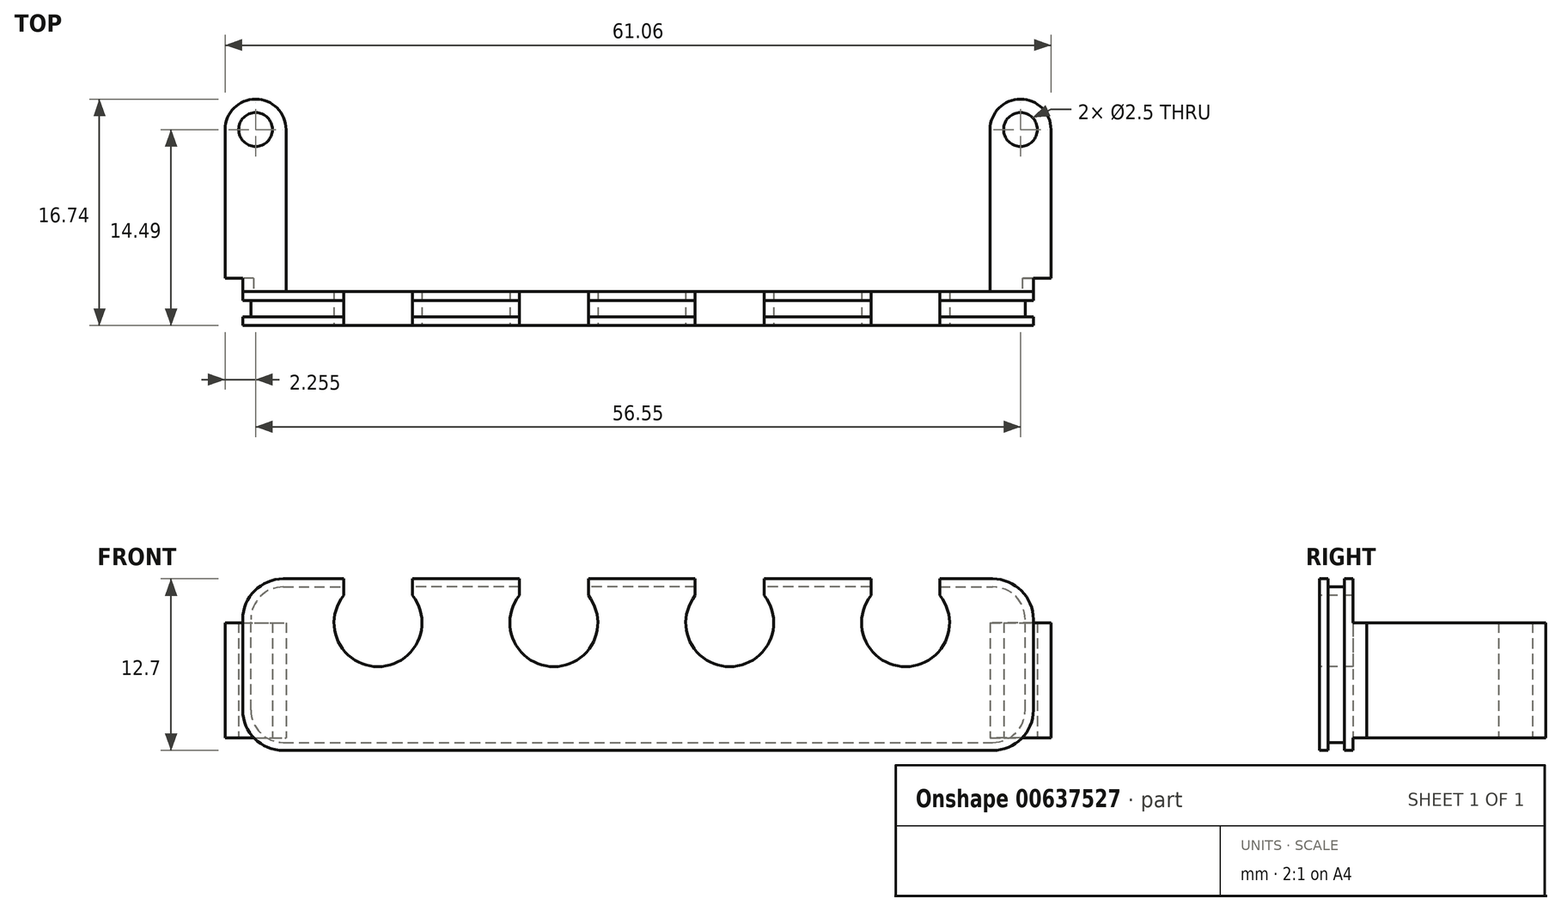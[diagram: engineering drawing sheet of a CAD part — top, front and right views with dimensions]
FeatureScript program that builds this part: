
annotation { "Feature Type Name" : "Feature", "Feature Type Description" : "" }
export const myFeature = defineFeature(function(context is Context, id is Id, definition is map)
    precondition{}
    {
        {
            var Q0;
            Q0=qCreatedBy(makeId("Front.planeOp"),FACE);
            var sketch = newSketch(context, id + "F0", { "sketchPlane" : qUnion([Q0])});
            skLineSegment(sketch, "E0.bottom", {"start": v(-26.22, -6.35) * mm, "end": v(26.23, -6.35) * mm});
            skLineSegment(sketch, "E0.top", {"start": v(-26.23, 6.35) * mm, "end": v(-21.77, 6.35) * mm});
            skLineSegment(sketch, "E0.left", {"start": v(-29.23, -3.35) * mm, "end": v(-29.23, 3.35) * mm});
            skLineSegment(sketch, "E0.right", {"start": v(29.23, -3.35) * mm, "end": v(29.23, 3.35) * mm});
            skPoint(sketch, "E0.middle", {"position": v(0, 0) * mm});
            skPoint(sketch, "E1.visualSharp", {"position": v(-29.23, 6.35) * mm});
            skArc(sketch, "E1.filletArc", {"start": v(-26.23, 6.35) * mm, "mid": v(-28.35, 5.47) * mm, "end": v(-29.23, 3.35) * mm});
            skPoint(sketch, "E2.visualSharp", {"position": v(-29.23, -6.35) * mm});
            skArc(sketch, "E2.filletArc", {"start": v(-29.23, -3.35) * mm, "mid": v(-28.35, -5.47) * mm, "end": v(-26.22, -6.35) * mm});
            skPoint(sketch, "E3.visualSharp", {"position": v(29.23, -6.35) * mm});
            skArc(sketch, "E3.filletArc", {"start": v(26.23, -6.35) * mm, "mid": v(28.35, -5.47) * mm, "end": v(29.23, -3.35) * mm});
            skPoint(sketch, "E4.visualSharp", {"position": v(29.23, 6.35) * mm});
            skArc(sketch, "E4.filletArc", {"start": v(29.23, 3.35) * mm, "mid": v(28.35, 5.47) * mm, "end": v(26.23, 6.35) * mm});
            skArc(sketch, "E5", {"start": v(-21.78, 5.11) * mm, "mid": v(-19.22, -0.15) * mm, "end": v(-16.67, 5.11) * mm});
            skArc(sketch, "E6", {"start": v(-8.78, 5.11) * mm, "mid": v(-6.22, -0.15) * mm, "end": v(-3.67, 5.11) * mm});
            skArc(sketch, "E7", {"start": v(4.22, 5.11) * mm, "mid": v(6.78, -0.15) * mm, "end": v(9.33, 5.11) * mm});
            skArc(sketch, "E8", {"start": v(17.22, 5.11) * mm, "mid": v(19.78, -0.15) * mm, "end": v(22.33, 5.11) * mm});
            skLineSegment(sketch, "E9.left", {"start": v(-21.77, 5.11) * mm, "end": v(-21.77, 6.35) * mm});
            skLineSegment(sketch, "E9.right", {"start": v(-16.67, 5.11) * mm, "end": v(-16.67, 6.35) * mm});
            skLineSegment(sketch, "E10.1.0.1", {"start": v(-8.77, 5.11) * mm, "end": v(-8.77, 6.35) * mm});
            skLineSegment(sketch, "E10.1.0.2", {"start": v(-3.67, 5.11) * mm, "end": v(-3.67, 6.35) * mm});
            skLineSegment(sketch, "E10.2.0.1", {"start": v(4.23, 5.11) * mm, "end": v(4.23, 6.35) * mm});
            skLineSegment(sketch, "E10.2.0.2", {"start": v(9.33, 5.11) * mm, "end": v(9.33, 6.35) * mm});
            skLineSegment(sketch, "E10.3.0.1", {"start": v(17.23, 5.11) * mm, "end": v(17.23, 6.35) * mm});
            skLineSegment(sketch, "E10.3.0.2", {"start": v(22.33, 5.11) * mm, "end": v(22.33, 6.35) * mm});
            skLineSegment(sketch, "E11.trimOffspring", {"start": v(-16.67, 6.35) * mm, "end": v(-8.77, 6.35) * mm});
            skLineSegment(sketch, "E12.trimOffspring", {"start": v(-3.67, 6.35) * mm, "end": v(4.23, 6.35) * mm});
            skLineSegment(sketch, "E13.trimOffspring", {"start": v(9.33, 6.35) * mm, "end": v(17.23, 6.35) * mm});
            skLineSegment(sketch, "E14.trimOffspring", {"start": v(22.33, 6.35) * mm, "end": v(26.23, 6.35) * mm});
            skSolve(sketch);
        }
        {
            var Q0;
            Q0=makeQuery(id+"F0.imprint","IMPRINT",FACE,{"disambiguationData":[TD([[makeQuery(id+"F0.imprint","IMPRINT",EDGE,{"derivedFrom":sQuery(id+"F0.wireOp",EDGE,"E0.bottom")}),1.0]])]});
            extrude(context, id + "F1", {"entities" : qUnion([Q0]), "oppositeDirection" : true, "depth" : 0.64 * mm, "offsetDistance" : 25 * mm});
        }
        {
            var Q0;
            Q0=makeQuery(id+"F1.opExtrude","CAP_FACE",FACE,{"disambiguationData":[OSD([sQuery(id+"F0.wireOp",EDGE,"E0.bottom"),sQuery(id+"F0.wireOp",EDGE,"E0.top"),sQuery(id+"F0.wireOp",EDGE,"E0.left"),sQuery(id+"F0.wireOp",EDGE,"E0.right"),sQuery(id+"F0.wireOp",EDGE,"E1.filletArc"),sQuery(id+"F0.wireOp",EDGE,"E2.filletArc"),sQuery(id+"F0.wireOp",EDGE,"E3.filletArc"),sQuery(id+"F0.wireOp",EDGE,"E4.filletArc"),sQuery(id+"F0.wireOp",EDGE,"E5"),sQuery(id+"F0.wireOp",EDGE,"E6"),sQuery(id+"F0.wireOp",EDGE,"E7"),sQuery(id+"F0.wireOp",EDGE,"E8"),sQuery(id+"F0.wireOp",EDGE,"E9.left"),sQuery(id+"F0.wireOp",EDGE,"E9.right"),sQuery(id+"F0.wireOp",EDGE,"E10.1.0.1"),sQuery(id+"F0.wireOp",EDGE,"E10.1.0.2"),sQuery(id+"F0.wireOp",EDGE,"E10.2.0.1"),sQuery(id+"F0.wireOp",EDGE,"E10.2.0.2"),sQuery(id+"F0.wireOp",EDGE,"E10.3.0.1"),sQuery(id+"F0.wireOp",EDGE,"E10.3.0.2"),sQuery(id+"F0.wireOp",EDGE,"E11.trimOffspring"),sQuery(id+"F0.wireOp",EDGE,"E12.trimOffspring"),sQuery(id+"F0.wireOp",EDGE,"E13.trimOffspring"),sQuery(id+"F0.wireOp",EDGE,"E14.trimOffspring")])],"isStart":false});
            var sketch = newSketch(context, id + "F2", { "sketchPlane" : qUnion([Q0])});
            skLineSegment(sketch, "E15.0", {"start": v(-22.33, 5.75) * mm, "end": v(-26.23, 5.75) * mm});
            skArc(sketch, "E15.1", {"start": v(-28.62, 3.35) * mm, "mid": v(-27.92, 5.05) * mm, "end": v(-26.23, 5.75) * mm});
            skLineSegment(sketch, "E15.2", {"start": v(-28.62, -3.35) * mm, "end": v(-28.62, 3.35) * mm});
            skArc(sketch, "E15.3", {"start": v(-26.23, -5.75) * mm, "mid": v(-27.92, -5.05) * mm, "end": v(-28.62, -3.35) * mm});
            skLineSegment(sketch, "E15.4", {"start": v(26.23, -5.75) * mm, "end": v(-26.23, -5.75) * mm});
            skLineSegment(sketch, "E15.5", {"start": v(26.23, 5.75) * mm, "end": v(21.77, 5.75) * mm});
            skArc(sketch, "E15.6", {"start": v(26.23, 5.75) * mm, "mid": v(27.92, 5.05) * mm, "end": v(28.62, 3.35) * mm});
            skLineSegment(sketch, "E15.7", {"start": v(28.62, -3.35) * mm, "end": v(28.62, 3.35) * mm});
            skArc(sketch, "E15.8", {"start": v(28.62, -3.35) * mm, "mid": v(27.92, -5.05) * mm, "end": v(26.23, -5.75) * mm});
            skArc(sketch, "E16", {"start": v(-22.33, 5.11) * mm, "mid": v(-19.78, -0.15) * mm, "end": v(-17.23, 5.11) * mm});
            skArc(sketch, "E17", {"start": v(-9.33, 5.11) * mm, "mid": v(-6.77, -0.15) * mm, "end": v(-4.23, 5.11) * mm});
            skArc(sketch, "E18", {"start": v(3.67, 5.11) * mm, "mid": v(6.23, -0.15) * mm, "end": v(8.77, 5.11) * mm});
            skArc(sketch, "E19", {"start": v(16.67, 5.11) * mm, "mid": v(19.23, -0.15) * mm, "end": v(21.77, 5.11) * mm});
            skLineSegment(sketch, "E20.left", {"start": v(-17.23, 5.75) * mm, "end": v(-17.23, 5.11) * mm});
            skLineSegment(sketch, "E20.right", {"start": v(-22.33, 5.75) * mm, "end": v(-22.33, 5.11) * mm});
            skLineSegment(sketch, "E21.left", {"start": v(-4.23, 5.75) * mm, "end": v(-4.23, 5.11) * mm});
            skLineSegment(sketch, "E21.right", {"start": v(-9.33, 5.75) * mm, "end": v(-9.33, 5.11) * mm});
            skLineSegment(sketch, "E22.left", {"start": v(8.77, 5.75) * mm, "end": v(8.77, 5.11) * mm});
            skLineSegment(sketch, "E22.right", {"start": v(3.67, 5.75) * mm, "end": v(3.67, 5.11) * mm});
            skLineSegment(sketch, "E23.left", {"start": v(21.77, 5.75) * mm, "end": v(21.78, 5.11) * mm});
            skLineSegment(sketch, "E23.right", {"start": v(16.67, 5.75) * mm, "end": v(16.67, 5.11) * mm});
            skLineSegment(sketch, "E24.trimOffspring", {"start": v(-17.23, 5.75) * mm, "end": v(-9.33, 5.75) * mm});
            skLineSegment(sketch, "E25.trimOffspring", {"start": v(-4.23, 5.75) * mm, "end": v(3.67, 5.75) * mm});
            skLineSegment(sketch, "E26.trimOffspring", {"start": v(8.77, 5.75) * mm, "end": v(16.67, 5.75) * mm});
            skSolve(sketch);
        }
        {
            var Q0;
            Q0=qSketchRegion(id+"F2",true);
            extrude(context, id + "F3", {"entities" : qUnion([Q0]), "operationType" : NewBodyOperationType.ADD, "depth" : 1.21 * mm, "offsetDistance" : 25 * mm});
        }
        {
            var Q0;
            Q0=makeQuery(id+"F3.opExtrude","CAP_FACE",FACE,{"disambiguationData":[OSD([sQuery(id+"F2.wireOp",EDGE,"E15.0"),sQuery(id+"F2.wireOp",EDGE,"E15.1"),sQuery(id+"F2.wireOp",EDGE,"E15.2"),sQuery(id+"F2.wireOp",EDGE,"E15.3"),sQuery(id+"F2.wireOp",EDGE,"E15.4"),sQuery(id+"F2.wireOp",EDGE,"E15.5"),sQuery(id+"F2.wireOp",EDGE,"E15.6"),sQuery(id+"F2.wireOp",EDGE,"E15.7"),sQuery(id+"F2.wireOp",EDGE,"E15.8"),sQuery(id+"F2.wireOp",EDGE,"E16"),sQuery(id+"F2.wireOp",EDGE,"E17"),sQuery(id+"F2.wireOp",EDGE,"E18"),sQuery(id+"F2.wireOp",EDGE,"E19"),sQuery(id+"F2.wireOp",EDGE,"E20.left"),sQuery(id+"F2.wireOp",EDGE,"E20.right"),sQuery(id+"F2.wireOp",EDGE,"E21.left"),sQuery(id+"F2.wireOp",EDGE,"E21.right"),sQuery(id+"F2.wireOp",EDGE,"E22.left"),sQuery(id+"F2.wireOp",EDGE,"E22.right"),sQuery(id+"F2.wireOp",EDGE,"E23.left"),sQuery(id+"F2.wireOp",EDGE,"E23.right"),sQuery(id+"F2.wireOp",EDGE,"E24.trimOffspring"),sQuery(id+"F2.wireOp",EDGE,"E25.trimOffspring"),sQuery(id+"F2.wireOp",EDGE,"E26.trimOffspring")])],"isStart":false});
            var sketch = newSketch(context, id + "F4", { "sketchPlane" : qUnion([Q0])});
            skLineSegment(sketch, "E27.bottom", {"start": v(-26.22, -6.35) * mm, "end": v(26.23, -6.35) * mm});
            skLineSegment(sketch, "E27.top", {"start": v(-26.23, 6.35) * mm, "end": v(-22.33, 6.35) * mm});
            skLineSegment(sketch, "E27.left", {"start": v(-29.23, -3.35) * mm, "end": v(-29.23, 3.35) * mm});
            skLineSegment(sketch, "E27.right", {"start": v(29.23, -3.35) * mm, "end": v(29.23, 3.35) * mm});
            skPoint(sketch, "E27.middle", {"position": v(0, 0) * mm});
            skPoint(sketch, "E28.visualSharp", {"position": v(-29.23, 6.35) * mm});
            skArc(sketch, "E28.filletArc", {"start": v(-26.23, 6.35) * mm, "mid": v(-28.35, 5.47) * mm, "end": v(-29.23, 3.35) * mm});
            skPoint(sketch, "E29.visualSharp", {"position": v(-29.23, -6.35) * mm});
            skArc(sketch, "E29.filletArc", {"start": v(-29.22, -3.35) * mm, "mid": v(-28.35, -5.47) * mm, "end": v(-26.22, -6.35) * mm});
            skPoint(sketch, "E30.visualSharp", {"position": v(29.23, -6.35) * mm});
            skArc(sketch, "E30.filletArc", {"start": v(26.23, -6.35) * mm, "mid": v(28.35, -5.47) * mm, "end": v(29.23, -3.35) * mm});
            skPoint(sketch, "E31.visualSharp", {"position": v(29.23, 6.35) * mm});
            skArc(sketch, "E31.filletArc", {"start": v(29.23, 3.35) * mm, "mid": v(28.35, 5.47) * mm, "end": v(26.23, 6.35) * mm});
            skArc(sketch, "E32", {"start": v(-22.33, 5.11) * mm, "mid": v(-19.77, -0.15) * mm, "end": v(-17.23, 5.11) * mm});
            skArc(sketch, "E33", {"start": v(-9.33, 5.11) * mm, "mid": v(-6.77, -0.15) * mm, "end": v(-4.22, 5.11) * mm});
            skArc(sketch, "E34", {"start": v(3.67, 5.11) * mm, "mid": v(6.23, -0.15) * mm, "end": v(8.78, 5.11) * mm});
            skArc(sketch, "E35", {"start": v(16.67, 5.11) * mm, "mid": v(19.23, -0.15) * mm, "end": v(21.78, 5.11) * mm});
            skLineSegment(sketch, "E36.left", {"start": v(-22.33, 5.11) * mm, "end": v(-22.33, 6.35) * mm});
            skLineSegment(sketch, "E36.right", {"start": v(-17.23, 5.11) * mm, "end": v(-17.23, 6.35) * mm});
            skLineSegment(sketch, "E37.1.0.1", {"start": v(-9.33, 5.11) * mm, "end": v(-9.33, 6.35) * mm});
            skLineSegment(sketch, "E37.1.0.2", {"start": v(-4.22, 5.11) * mm, "end": v(-4.22, 6.35) * mm});
            skLineSegment(sketch, "E37.2.0.1", {"start": v(3.67, 5.11) * mm, "end": v(3.67, 6.35) * mm});
            skLineSegment(sketch, "E37.2.0.2", {"start": v(8.78, 5.11) * mm, "end": v(8.78, 6.35) * mm});
            skLineSegment(sketch, "E37.3.0.1", {"start": v(16.67, 5.11) * mm, "end": v(16.67, 6.35) * mm});
            skLineSegment(sketch, "E37.3.0.2", {"start": v(21.78, 5.11) * mm, "end": v(21.78, 6.35) * mm});
            skLineSegment(sketch, "E38.trimOffspring", {"start": v(-17.23, 6.35) * mm, "end": v(-9.33, 6.35) * mm});
            skLineSegment(sketch, "E39.trimOffspring", {"start": v(-4.22, 6.35) * mm, "end": v(3.67, 6.35) * mm});
            skLineSegment(sketch, "E40.trimOffspring", {"start": v(8.78, 6.35) * mm, "end": v(16.67, 6.35) * mm});
            skLineSegment(sketch, "E41.trimOffspring", {"start": v(21.78, 6.35) * mm, "end": v(26.23, 6.35) * mm});
            skSolve(sketch);
        }
        {
            var Q0;
            Q0=qSketchRegion(id+"F4",true);
            extrude(context, id + "F5", {"entities" : qUnion([Q0]), "operationType" : NewBodyOperationType.ADD, "depth" : 0.64 * mm, "offsetDistance" : 25 * mm});
        }
        {
            var Q0;
            Q0=makeQuery(id+"F5.opExtrude","SWEPT_FACE",FACE,{"disambiguationData":[OSD([sQuery(id+"F4.wireOp",EDGE,"E27.bottom")])]});
            cPlane(context, id + "F6", {"entities" : qUnion([Q0]), "cplaneType" : CPlaneType.OFFSET, "offset" : 0.95 * mm, "oppositeDirection" : true, "width" : 150 * mm, "height" : 150 * mm});
        }
        {
            var Q0;
            Q0=qCreatedBy(id+"F6.planeOp",FACE);
            var sketch = newSketch(context, id + "F7", { "sketchPlane" : qUnion([Q0])});
            skLineSegment(sketch, "E42.bottom", {"start": v(29.23, -2.5) * mm, "end": v(26.02, -2.5) * mm});
            skLineSegment(sketch, "E42.left", {"start": v(29.23, -2.5) * mm, "end": v(29.23, -3.49) * mm});
            skLineSegment(sketch, "E42.right", {"start": v(26.02, -2.5) * mm, "end": v(26.02, -3.49) * mm});
            skLineSegment(sketch, "E43.bottom", {"start": v(29.23, -3.49) * mm, "end": v(30.52, -3.49) * mm});
            skLineSegment(sketch, "E43.left", {"start": v(26.02, -3.49) * mm, "end": v(26.02, -14.5) * mm});
            skLineSegment(sketch, "E43.right", {"start": v(30.52, -3.49) * mm, "end": v(30.52, -14.5) * mm});
            skArc(sketch, "E44", {"start": v(26.02, -14.5) * mm, "mid": v(28.28, -16.74) * mm, "end": v(30.53, -14.5) * mm});
            skCircle(sketch, "E45", {"center": v(28.28, -14.5) * mm, "radius": 1.25 * mm});
            skLineSegment(sketch, "E46.MirrorCS", {"start": v(-26.02, -3.49) * mm, "end": v(-26.02, -14.5) * mm});
            skLineSegment(sketch, "E47.MirrorCS", {"start": v(-30.52, -3.49) * mm, "end": v(-30.52, -14.5) * mm});
            skCircle(sketch, "E48.MirrorC", {"center": v(-28.28, -14.5) * mm, "radius": 1.25 * mm});
            skArc(sketch, "E49.MirrorCS", {"start": v(-26.02, -14.5) * mm, "mid": v(-28.28, -16.74) * mm, "end": v(-30.53, -14.5) * mm});
            skLineSegment(sketch, "E50.MirrorCS", {"start": v(-29.23, -3.49) * mm, "end": v(-30.52, -3.49) * mm});
            skLineSegment(sketch, "E51.MirrorCS", {"start": v(-29.23, -2.5) * mm, "end": v(-29.23, -3.49) * mm});
            skLineSegment(sketch, "E52.MirrorCS", {"start": v(-29.23, -2.5) * mm, "end": v(-26.02, -2.5) * mm});
            skLineSegment(sketch, "E53.MirrorCS", {"start": v(-26.02, -2.5) * mm, "end": v(-26.02, -3.49) * mm});
            skPoint(sketch, "E54.MirrorCS.end.orphan", {"position": v(-26.02, -3.49) * mm});
            skPoint(sketch, "E54.MirrorCS.start.orphan", {"position": v(-29.23, -3.49) * mm});
            skSolve(sketch);
        }
        {
            var Q0;
            Q0=qSketchRegion(id+"F7",true);
            extrude(context, id + "F8", {"entities" : qUnion([Q0]), "operationType" : NewBodyOperationType.ADD, "oppositeDirection" : true, "depth" : 8.5 * mm, "offsetDistance" : 25 * mm});
        }
        {
            var Q0;
            Q0=makeQuery(id+"F8.opExtrude","SWEPT_FACE",FACE,{"disambiguationData":[OSD([sQuery(id+"F7.wireOp",EDGE,"E42.bottom")])]});
            var Q1;
            Q1=makeQuery(id+"F8.opExtrude","SWEPT_FACE",FACE,{"disambiguationData":[OSD([sQuery(id+"F7.wireOp",EDGE,"E52.MirrorCS")])]});
            extrude(context, id + "F9", {"entities" : qUnion([Q0, Q1]), "operationType" : NewBodyOperationType.REMOVE, "oppositeDirection" : true, "depth" : 1 * mm, "offsetDistance" : 25 * mm});
        }
    });
